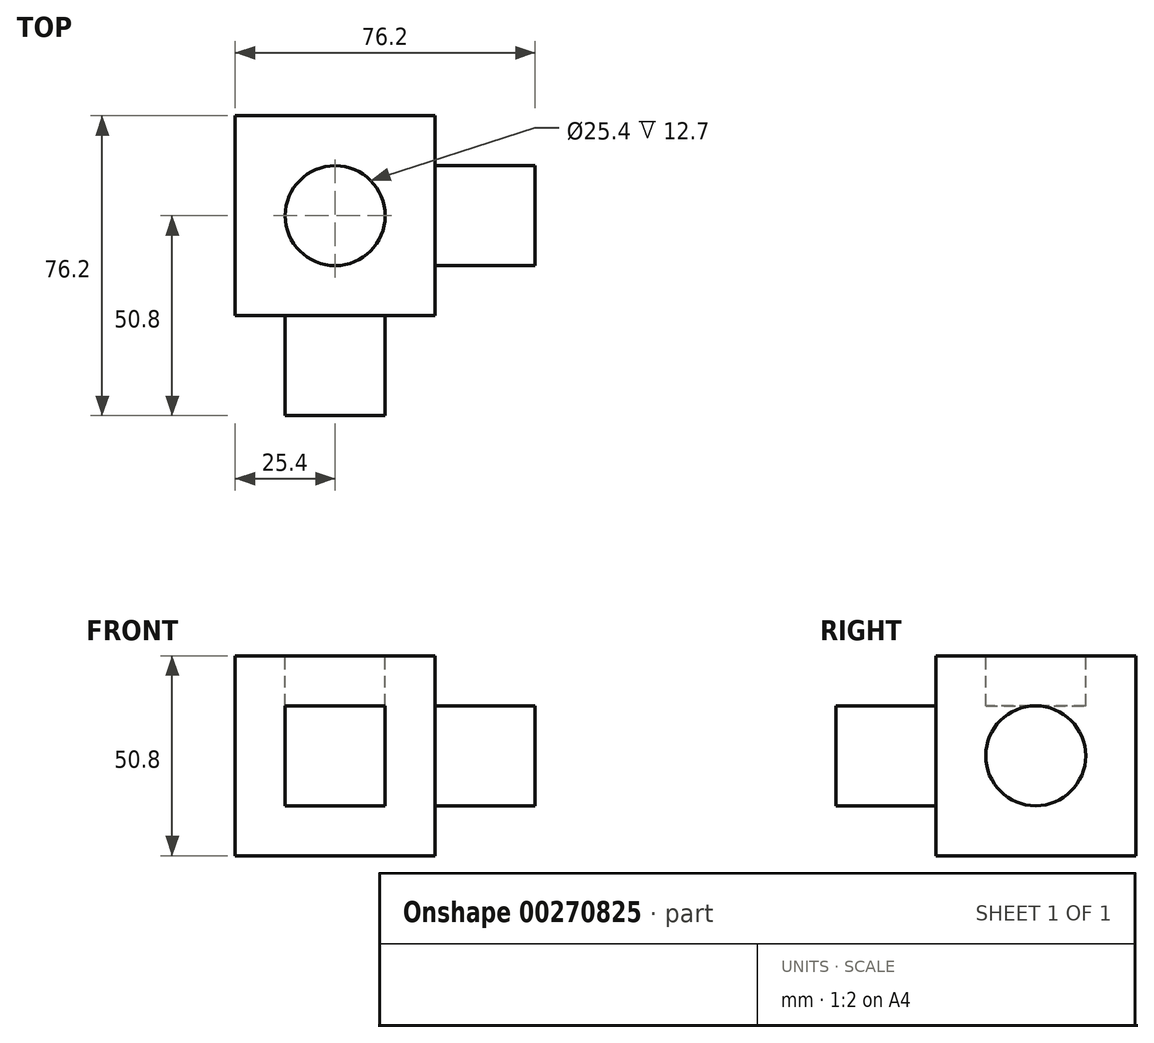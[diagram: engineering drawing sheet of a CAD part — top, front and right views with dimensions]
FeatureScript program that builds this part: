
annotation { "Feature Type Name" : "Feature", "Feature Type Description" : "" }
export const myFeature = defineFeature(function(context is Context, id is Id, definition is map)
    precondition{}
    {
        {
            var Q0;
            Q0=qCreatedBy(makeId("Front.planeOp"),FACE);
            var sketch = newSketch(context, id + "F0", { "sketchPlane" : qUnion([Q0])});
            skLineSegment(sketch, "E0.bottom", {"start": v(0, 0) * mm, "end": v(-50.8, 0) * mm});
            skLineSegment(sketch, "E0.top", {"start": v(0, 50.8) * mm, "end": v(-50.8, 50.8) * mm});
            skLineSegment(sketch, "E0.left", {"start": v(0, 0) * mm, "end": v(0, 50.8) * mm});
            skLineSegment(sketch, "E0.right", {"start": v(-50.8, 0) * mm, "end": v(-50.8, 50.8) * mm});
            skSolve(sketch);
        }
        {
            var Q0;
            Q0 = qSketchRegion(id + "F0", true);
            extrude(context, id + "F1", {"entities" : qUnion([Q0]), "depth" : 50.8 * mm});
        }
        {
            var Q0;
            Q0=makeQuery(id+"F1.opExtrude","CAP_FACE",FACE,{"disambiguationData":[OSD([sQuery(id+"F0.wireOp",EDGE,"E0.bottom"),sQuery(id+"F0.wireOp",EDGE,"E0.top"),sQuery(id+"F0.wireOp",EDGE,"E0.left"),sQuery(id+"F0.wireOp",EDGE,"E0.right")])],"isStart":false});
            var sketch = newSketch(context, id + "F2", { "sketchPlane" : qUnion([Q0])});
            skLineSegment(sketch, "E1.bottom", {"start": v(-38.1, 38.1) * mm, "end": v(-12.7, 38.1) * mm});
            skLineSegment(sketch, "E1.top", {"start": v(-38.1, 12.7) * mm, "end": v(-12.7, 12.7) * mm});
            skLineSegment(sketch, "E1.left", {"start": v(-38.1, 38.1) * mm, "end": v(-38.1, 12.7) * mm});
            skLineSegment(sketch, "E1.right", {"start": v(-12.7, 38.1) * mm, "end": v(-12.7, 12.7) * mm});
            skSolve(sketch);
        }
        {
            var Q0;
            Q0 = qSketchRegion(id + "F2", true);
            extrude(context, id + "F3", {"entities" : qUnion([Q0]), "operationType" : NewBodyOperationType.ADD, "depth" : 25.4 * mm});
        }
        {
            var Q0;
            Q0=makeQuery(id+"F1.opExtrude","SWEPT_FACE",FACE,{"disambiguationData":[OSD([sQuery(id+"F0.wireOp",EDGE,"E0.left")])]});
            var sketch = newSketch(context, id + "F4", { "sketchPlane" : qUnion([Q0])});
            skCircle(sketch, "E2", {"center": v(-25.4, 25.4) * mm, "radius": 12.7 * mm});
            skSolve(sketch);
        }
        {
            var Q0;
            Q0 = qSketchRegion(id + "F4", true);
            extrude(context, id + "F5", {"entities" : qUnion([Q0]), "operationType" : NewBodyOperationType.ADD, "depth" : 25.4 * mm});
        }
        {
            var Q0;
            Q0=makeQuery(id+"F1.opExtrude","SWEPT_FACE",FACE,{"disambiguationData":[OSD([sQuery(id+"F0.wireOp",EDGE,"E0.top")])]});
            var sketch = newSketch(context, id + "F6", { "sketchPlane" : qUnion([Q0])});
            skCircle(sketch, "E3", {"center": v(-25.4, -25.4) * mm, "radius": 12.7 * mm});
            skSolve(sketch);
        }
        {
            var Q0;
            Q0 = qSketchRegion(id + "F6", true);
            extrude(context, id + "F7", {"entities" : qUnion([Q0]), "operationType" : NewBodyOperationType.REMOVE, "oppositeDirection" : true, "depth" : 12.7 * mm});
        }
    });
